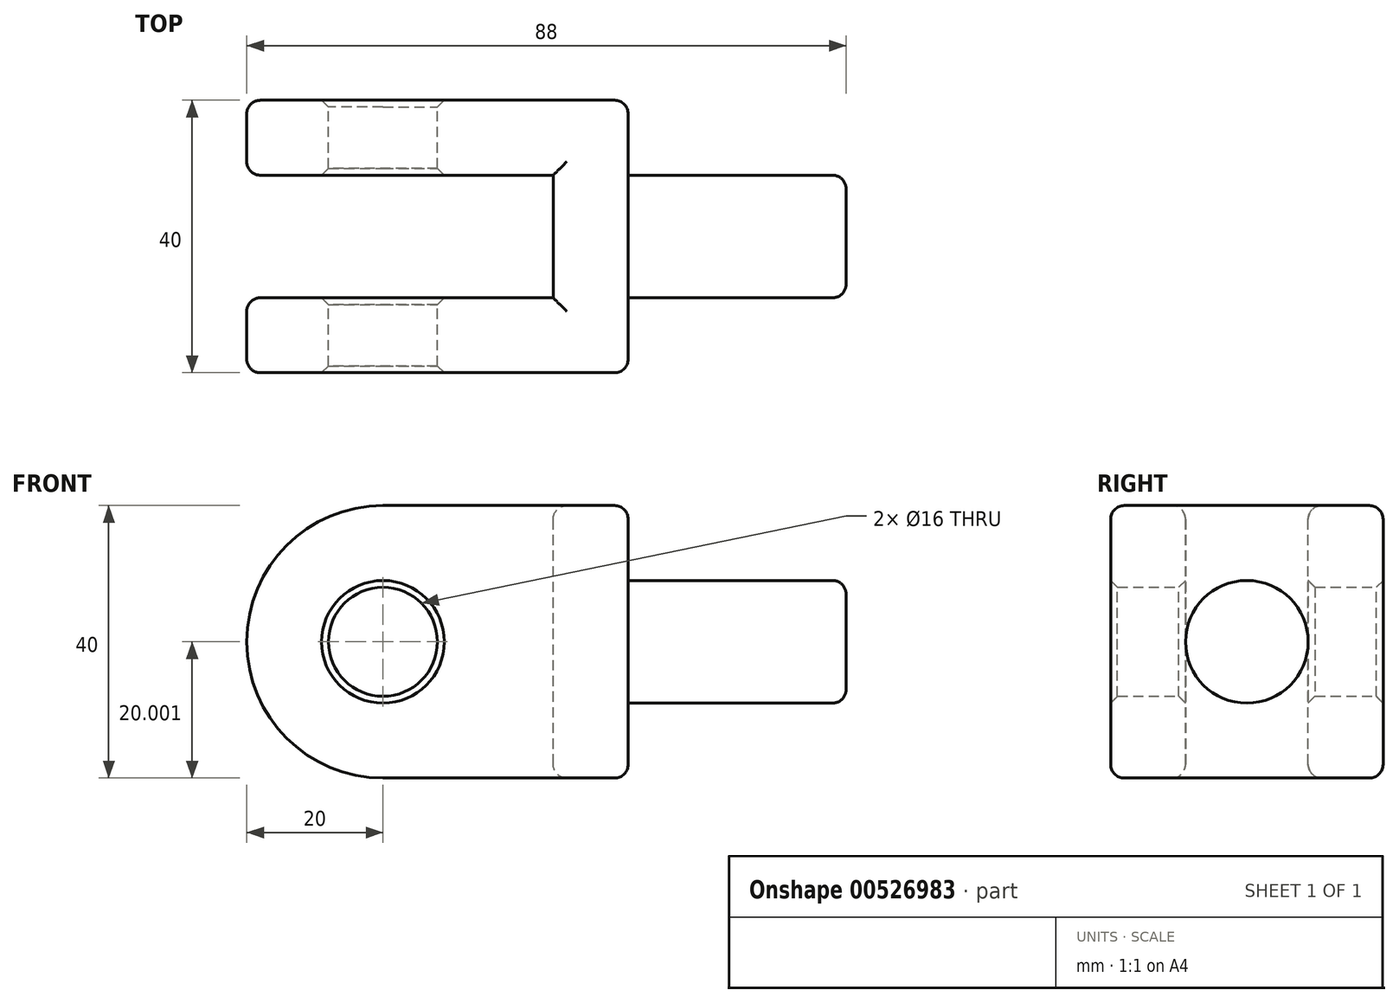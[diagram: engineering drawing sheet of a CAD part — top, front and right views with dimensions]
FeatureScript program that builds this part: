
annotation { "Feature Type Name" : "Feature", "Feature Type Description" : "" }
export const myFeature = defineFeature(function(context is Context, id is Id, definition is map)
    precondition{}
    {
        {
            var Q0;
            Q0=qCreatedBy(makeId("Front.planeOp"),FACE);
            var sketch = newSketch(context, id + "F0", { "sketchPlane" : qUnion([Q0])});
            skLineSegment(sketch, "E0", {"start": v(11, 12.93) * mm, "end": v(11, -27.07) * mm});
            skLineSegment(sketch, "E1", {"start": v(11, -27.07) * mm, "end": v(0, -27.07) * mm});
            skLineSegment(sketch, "E2", {"start": v(0, -27.07) * mm, "end": v(0, 12.93) * mm});
            skLineSegment(sketch, "E3", {"start": v(0, 12.93) * mm, "end": v(11, 12.93) * mm});
            skLineSegment(sketch, "E4", {"start": v(0, 12.93) * mm, "end": v(-25, 12.93) * mm});
            skLineSegment(sketch, "E5", {"start": v(-25, 12.93) * mm, "end": v(-25, -27.07) * mm});
            skLineSegment(sketch, "E6", {"start": v(-25, -27.07) * mm, "end": v(0, -27.07) * mm});
            skArc(sketch, "E7", {"start": v(-25, 12.93) * mm, "mid": v(-45, -7.07) * mm, "end": v(-25, -27.07) * mm});
            skCircle(sketch, "E8", {"center": v(-25, -7.07) * mm, "radius": 8 * mm});
            skSolve(sketch);
        }
        {
            var Q0;
            Q0 = qSketchRegion(id + "F0", true);
            extrude(context, id + "F1", {"entities" : qUnion([Q0]), "depth" : 11 * mm, "offsetDistance" : 25.4 * mm});
        }
        {
            var Q0;
            Q0=makeQuery(id+"F1.opExtrude","CAP_FACE",FACE,{"disambiguationData":[OSD([sQuery(id+"F0.wireOp",EDGE,"E0"),sQuery(id+"F0.wireOp",EDGE,"E1"),sQuery(id+"F0.wireOp",EDGE,"E3"),sQuery(id+"F0.wireOp",EDGE,"E4"),sQuery(id+"F0.wireOp",EDGE,"E6"),sQuery(id+"F0.wireOp",EDGE,"E7"),sQuery(id+"F0.wireOp",EDGE,"E8")])],"isStart":false});
            var sketch = newSketch(context, id + "F2", { "sketchPlane" : qUnion([Q0])});
            skLineSegment(sketch, "E9", {"start": v(0, -27.07) * mm, "end": v(0, 12.93) * mm});
            skPoint(sketch, "E9.startSnap0", {"position": v(-7, -27.07) * mm});
            skLineSegment(sketch, "E10", {"start": v(0, 12.93) * mm, "end": v(11, 12.93) * mm});
            skLineSegment(sketch, "E11", {"start": v(11, 12.93) * mm, "end": v(11, -27.07) * mm});
            skLineSegment(sketch, "E12", {"start": v(11, -27.07) * mm, "end": v(0, -27.07) * mm});
            skSolve(sketch);
        }
        {
            var Q0;
            Q0 = qSketchRegion(id + "F2", true);
            extrude(context, id + "F3", {"entities" : qUnion([Q0]), "operationType" : NewBodyOperationType.ADD, "oppositeDirection" : true, "depth" : 40 * mm, "offsetDistance" : 25.4 * mm});
        }
        {
            var Q0;
            Q0=makeQuery(id+"F3.boolean.opBoolean","MERGE",FACE,{"derivedFrom":[makeQuery(id+"F1.opExtrude","SWEPT_FACE",FACE,{"disambiguationData":[OSD([sQuery(id+"F0.wireOp",EDGE,"E0")])]}),makeQuery(id+"F3.opExtrude","SWEPT_FACE",FACE,{"disambiguationData":[OSD([sQuery(id+"F2.wireOp",EDGE,"E11")])]})]});
            var sketch = newSketch(context, id + "F4", { "sketchPlane" : qUnion([Q0])});
            skCircle(sketch, "E13", {"center": v(9, -7.07) * mm, "radius": 9 * mm});
            skPoint(sketch, "E13.centerSnap0", {"position": v(-11, -7.07) * mm});
            skPoint(sketch, "E13.centerSnap1", {"position": v(9, -27.07) * mm});
            skSolve(sketch);
        }
        {
            var Q0;
            Q0 = qSketchRegion(id + "F4", true);
            extrude(context, id + "F5", {"entities" : qUnion([Q0]), "operationType" : NewBodyOperationType.ADD, "depth" : 32 * mm, "offsetDistance" : 25.4 * mm});
        }
        {
            var Q0;
            Q0=makeQuery(id+"F3.opExtrude","CAP_FACE",FACE,{"disambiguationData":[OSD([sQuery(id+"F2.wireOp",EDGE,"E9"),sQuery(id+"F2.wireOp",EDGE,"E10"),sQuery(id+"F2.wireOp",EDGE,"E11"),sQuery(id+"F2.wireOp",EDGE,"E12")])],"isStart":false});
            var sketch = newSketch(context, id + "F6", { "sketchPlane" : qUnion([Q0])});
            skLineSegment(sketch, "E14", {"start": v(0, 12.93) * mm, "end": v(25, 12.93) * mm});
            skLineSegment(sketch, "E15", {"start": v(25, 12.93) * mm, "end": v(25, -27.07) * mm});
            skLineSegment(sketch, "E16", {"start": v(25, -27.07) * mm, "end": v(0, -27.07) * mm});
            skLineSegment(sketch, "E17", {"start": v(0, -27.07) * mm, "end": v(0, 12.93) * mm});
            skArc(sketch, "E18", {"start": v(25, -27.07) * mm, "mid": v(45, -7.07) * mm, "end": v(25, 12.93) * mm});
            skCircle(sketch, "E19", {"center": v(25, -7.07) * mm, "radius": 8 * mm});
            skSolve(sketch);
        }
        {
            var Q0;
            Q0 = qSketchRegion(id + "F6", true);
            extrude(context, id + "F7", {"entities" : qUnion([Q0]), "operationType" : NewBodyOperationType.ADD, "oppositeDirection" : true, "depth" : 11 * mm, "offsetDistance" : 25.4 * mm});
        }
        {
            var Q0;
            Q0=makeQuery(id+"F1.opExtrude","CAP_EDGE",EDGE,{"disambiguationData":[OSD([sQuery(id+"F0.wireOp",EDGE,"E8")])],"isStart":false});
            var Q1;
            Q1=makeQuery(id+"F1.opExtrude","CAP_EDGE",EDGE,{"disambiguationData":[OSD([sQuery(id+"F0.wireOp",EDGE,"E8")])],"isStart":true});
            var Q2;
            Q2=makeQuery(id+"F7.opExtrude","CAP_EDGE",EDGE,{"disambiguationData":[OSD([sQuery(id+"F6.wireOp",EDGE,"E19")])],"isStart":false});
            var Q3;
            Q3=makeQuery(id+"F7.opExtrude","CAP_EDGE",EDGE,{"disambiguationData":[OSD([sQuery(id+"F6.wireOp",EDGE,"E19")])],"isStart":true});
            chamfer(context, id + "F8", {"entities" : qUnion([Q0, Q1, Q2, Q3]), "chamferType" : ChamferType.OFFSET_ANGLE, "width" : 1 * mm, "oppositeDirection" : false, "angle" : 45 * degree, "tangentPropagation" : true});
        }
        {
            var Q0;
            Q0=makeQuery(id+"F1.opExtrude","CAP_EDGE",EDGE,{"disambiguationData":[OSD([sQuery(id+"F0.wireOp",EDGE,"E7")])],"isStart":false});
            var Q1;
            Q1=makeQuery(id+"F1.opExtrude","CAP_EDGE",EDGE,{"disambiguationData":[OSD([sQuery(id+"F0.wireOp",EDGE,"E7")])],"isStart":true});
            var Q2;
            Q2=makeQuery(id+"F3.boolean.opBoolean","MERGE",EDGE,{"derivedFrom":[makeQuery(id+"F1.opExtrude","SWEPT_EDGE",EDGE,{"disambiguationData":[OSD([sQuery(id+"F0.wireOp",EDGE,"E0"),sQuery(id+"F0.wireOp",EDGE,"E1")])]}),makeQuery(id+"F3.opExtrude","SWEPT_EDGE",EDGE,{"disambiguationData":[OSD([sQuery(id+"F2.wireOp",EDGE,"E11"),sQuery(id+"F2.wireOp",EDGE,"E12")])]})]});
            var Q3;
            Q3=makeQuery(id+"F7.boolean.opBoolean","MERGE",EDGE,{"derivedFrom":[makeQuery(id+"F3.opExtrude","CAP_EDGE",EDGE,{"disambiguationData":[OSD([sQuery(id+"F2.wireOp",EDGE,"E12")])],"isStart":false}),makeQuery(id+"F7.opExtrude","CAP_EDGE",EDGE,{"disambiguationData":[OSD([sQuery(id+"F6.wireOp",EDGE,"E16")])],"isStart":true})]});
            var Q4;
            Q4=makeQuery(id+"F7.opExtrude","CAP_EDGE",EDGE,{"disambiguationData":[OSD([sQuery(id+"F6.wireOp",EDGE,"E16")])],"isStart":false});
            var Q5;
            Q5=makeQuery(id+"F3.opExtrude","SWEPT_EDGE",EDGE,{"disambiguationData":[OSD([sQuery(id+"F0.wireOp",EDGE,"E1"),sQuery(id+"F0.wireOp",EDGE,"E6"),sQuery(id+"F2.wireOp",EDGE,"E9"),sQuery(id+"F2.wireOp",EDGE,"E12")])]});
            var Q6;
            Q6=makeQuery(id+"F3.opExtrude","CAP_EDGE",EDGE,{"disambiguationData":[OSD([sQuery(id+"F2.wireOp",EDGE,"E11")])],"isStart":false});
            var Q7;
            Q7=makeQuery(id+"F1.opExtrude","CAP_EDGE",EDGE,{"disambiguationData":[OSD([sQuery(id+"F0.wireOp",EDGE,"E0")])],"isStart":false});
            var Q8;
            Q8=makeQuery(id+"F5.opExtrude","CAP_EDGE",EDGE,{"disambiguationData":[OSD([sQuery(id+"F4.wireOp",EDGE,"E13")])],"isStart":false});
            var Q9;
            Q9=makeQuery(id+"F3.boolean.opBoolean","MERGE",EDGE,{"derivedFrom":[makeQuery(id+"F1.opExtrude","SWEPT_EDGE",EDGE,{"disambiguationData":[OSD([sQuery(id+"F0.wireOp",EDGE,"E0"),sQuery(id+"F0.wireOp",EDGE,"E3")])]}),makeQuery(id+"F3.opExtrude","SWEPT_EDGE",EDGE,{"disambiguationData":[OSD([sQuery(id+"F2.wireOp",EDGE,"E10"),sQuery(id+"F2.wireOp",EDGE,"E11")])]})]});
            var Q10;
            Q10=makeQuery(id+"F3.opExtrude","SWEPT_EDGE",EDGE,{"disambiguationData":[OSD([sQuery(id+"F0.wireOp",EDGE,"E3"),sQuery(id+"F0.wireOp",EDGE,"E4"),sQuery(id+"F2.wireOp",EDGE,"E9"),sQuery(id+"F2.wireOp",EDGE,"E10")])]});
            fillet(context, id + "F9", {"entities" : qUnion([Q0, Q1, Q2, Q3, Q4, Q5, Q6, Q7, Q8, Q9, Q10]), "radius" : 2 * mm, "tangentPropagation" : true, "allowEdgeOverflow" : false});
        }
    });
